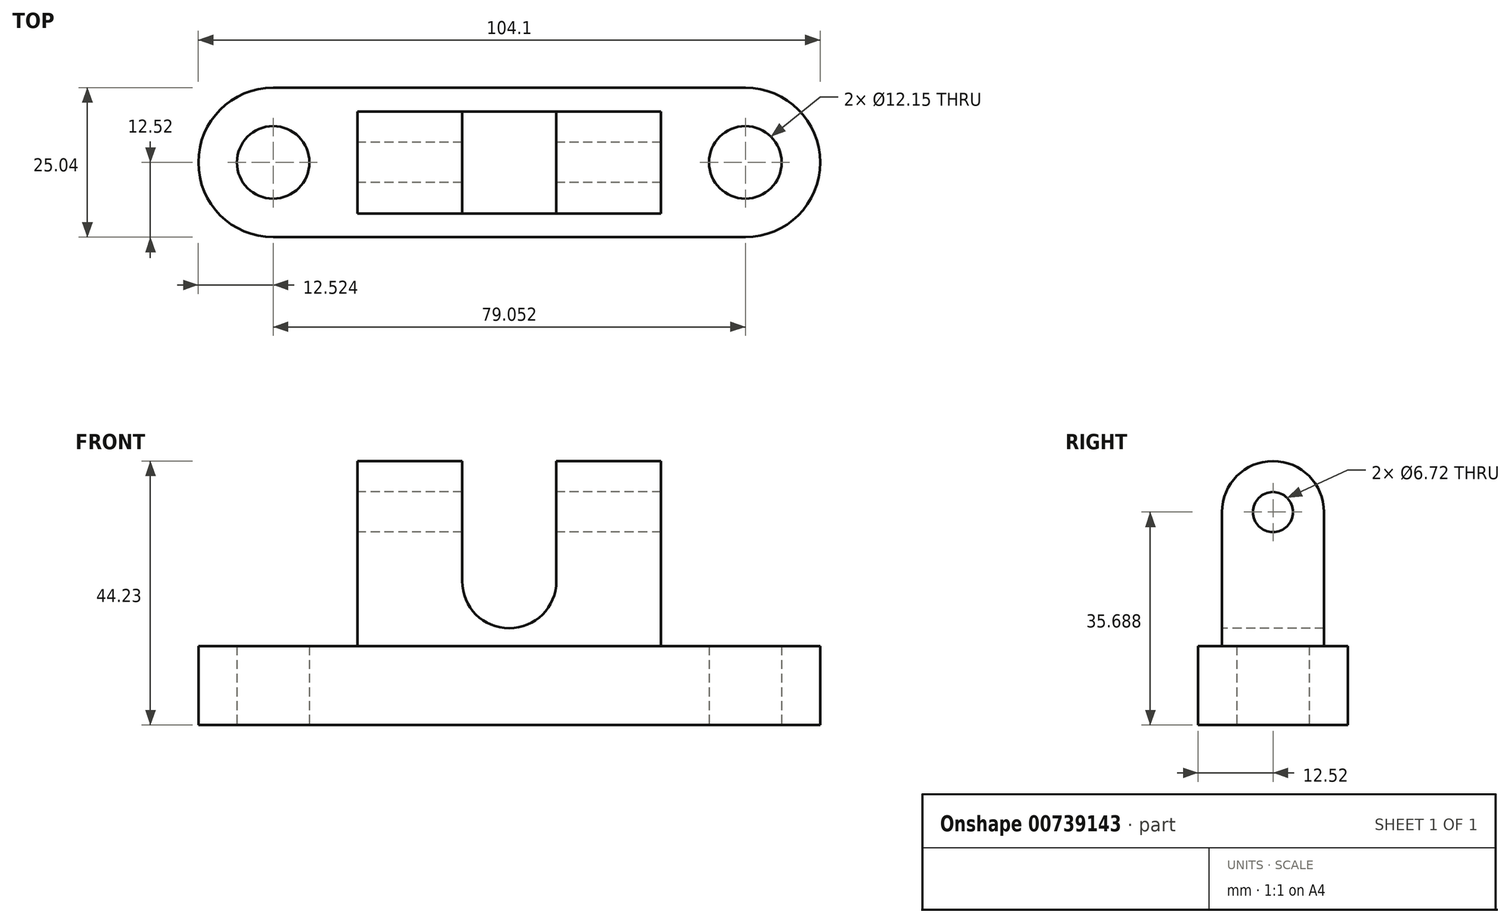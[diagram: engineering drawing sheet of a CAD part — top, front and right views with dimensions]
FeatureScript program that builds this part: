
annotation { "Feature Type Name" : "Feature", "Feature Type Description" : "" }
export const myFeature = defineFeature(function(context is Context, id is Id, definition is map)
    precondition{}
    {
        {
            var Q0;
            Q0=qCreatedBy(makeId("Top.planeOp"),FACE);
            var sketch = newSketch(context, id + "F0", { "sketchPlane" : qUnion([Q0])});
            skLineSegment(sketch, "E0.bottom", {"start": v(39.53, 12.52) * mm, "end": v(-39.53, 12.52) * mm});
            skLineSegment(sketch, "E0.top", {"start": v(39.53, -12.52) * mm, "end": v(-39.53, -12.52) * mm});
            skLineSegment(sketch, "E0.left", {"start": v(39.53, 12.52) * mm, "end": v(39.53, -12.52) * mm});
            skLineSegment(sketch, "E0.right", {"start": v(-39.53, 12.52) * mm, "end": v(-39.53, -12.52) * mm});
            skPoint(sketch, "E0.middle", {"position": v(0, 0) * mm});
            skCircle(sketch, "E1", {"center": v(-39.53, 0) * mm, "radius": 12.52 * mm});
            skCircle(sketch, "E2", {"center": v(39.53, 0) * mm, "radius": 12.52 * mm});
            skCircle(sketch, "E3", {"center": v(-39.53, 0) * mm, "radius": 6.07 * mm});
            skCircle(sketch, "E4", {"center": v(39.53, 0) * mm, "radius": 6.07 * mm});
            skSolve(sketch);
        }
        {
            var Q0;
            Q0 = qSketchRegion(id + "F0", true);
            extrude(context, id + "F1", {"entities" : qUnion([Q0]), "depth" : 13.2 * mm, "offsetDistance" : 25.4 * mm});
        }
        {
            var Q0;
            Q0=qCreatedBy(makeId("Right.planeOp"),FACE);
            var sketch = newSketch(context, id + "F2", { "sketchPlane" : qUnion([Q0])});
            skCircle(sketch, "E5", {"center": v(0, 35.69) * mm, "radius": 3.36 * mm});
            skCircle(sketch, "E6", {"center": v(0, 35.69) * mm, "radius": 8.54 * mm});
            skLineSegment(sketch, "E7.bottom", {"start": v(-8.54, 35.69) * mm, "end": v(8.54, 35.69) * mm});
            skLineSegment(sketch, "E7.top", {"start": v(-8.54, 0) * mm, "end": v(8.54, 0) * mm});
            skLineSegment(sketch, "E7.left", {"start": v(-8.54, 35.69) * mm, "end": v(-8.54, 0) * mm});
            skLineSegment(sketch, "E7.right", {"start": v(8.54, 35.69) * mm, "end": v(8.54, 0) * mm});
            skSolve(sketch);
        }
        {
            var Q0;
            Q0 = qSketchRegion(id + "F2", true);
            extrude(context, id + "F3", {"entities" : qUnion([Q0]), "operationType" : NewBodyOperationType.ADD, "depth" : 25.4 * mm, "offsetDistance" : 25.4 * mm});
        }
        {
            var Q0;
            Q0 = qSketchRegion(id + "F2", true);
            extrude(context, id + "F4", {"entities" : qUnion([Q0]), "operationType" : NewBodyOperationType.ADD, "oppositeDirection" : true, "depth" : 25.4 * mm, "offsetDistance" : 25.4 * mm});
        }
        {
            var Q0;
            Q0=qCreatedBy(makeId("Front.planeOp"),FACE);
            var sketch = newSketch(context, id + "F5", { "sketchPlane" : qUnion([Q0])});
            skCircle(sketch, "E8", {"center": v(0, 24.1) * mm, "radius": 7.88 * mm});
            skLineSegment(sketch, "E9.bottom", {"start": v(-7.88, 24.1) * mm, "end": v(7.88, 24.1) * mm});
            skLineSegment(sketch, "E9.top", {"start": v(-7.88, 49.5) * mm, "end": v(7.88, 49.5) * mm});
            skLineSegment(sketch, "E9.left", {"start": v(-7.88, 24.1) * mm, "end": v(-7.88, 49.5) * mm});
            skLineSegment(sketch, "E9.right", {"start": v(7.88, 24.1) * mm, "end": v(7.88, 49.5) * mm});
            skSolve(sketch);
        }
        {
            var Q0;
            Q0 = qSketchRegion(id + "F5", true);
            extrude(context, id + "F6", {"entities" : qUnion([Q0]), "operationType" : NewBodyOperationType.REMOVE, "oppositeDirection" : true, "depth" : 25.4 * mm, "offsetDistance" : 25.4 * mm});
        }
        {
            var Q0;
            Q0 = qSketchRegion(id + "F5", true);
            extrude(context, id + "F7", {"entities" : qUnion([Q0]), "operationType" : NewBodyOperationType.REMOVE, "depth" : 25.4 * mm, "offsetDistance" : 25.4 * mm});
        }
    });
